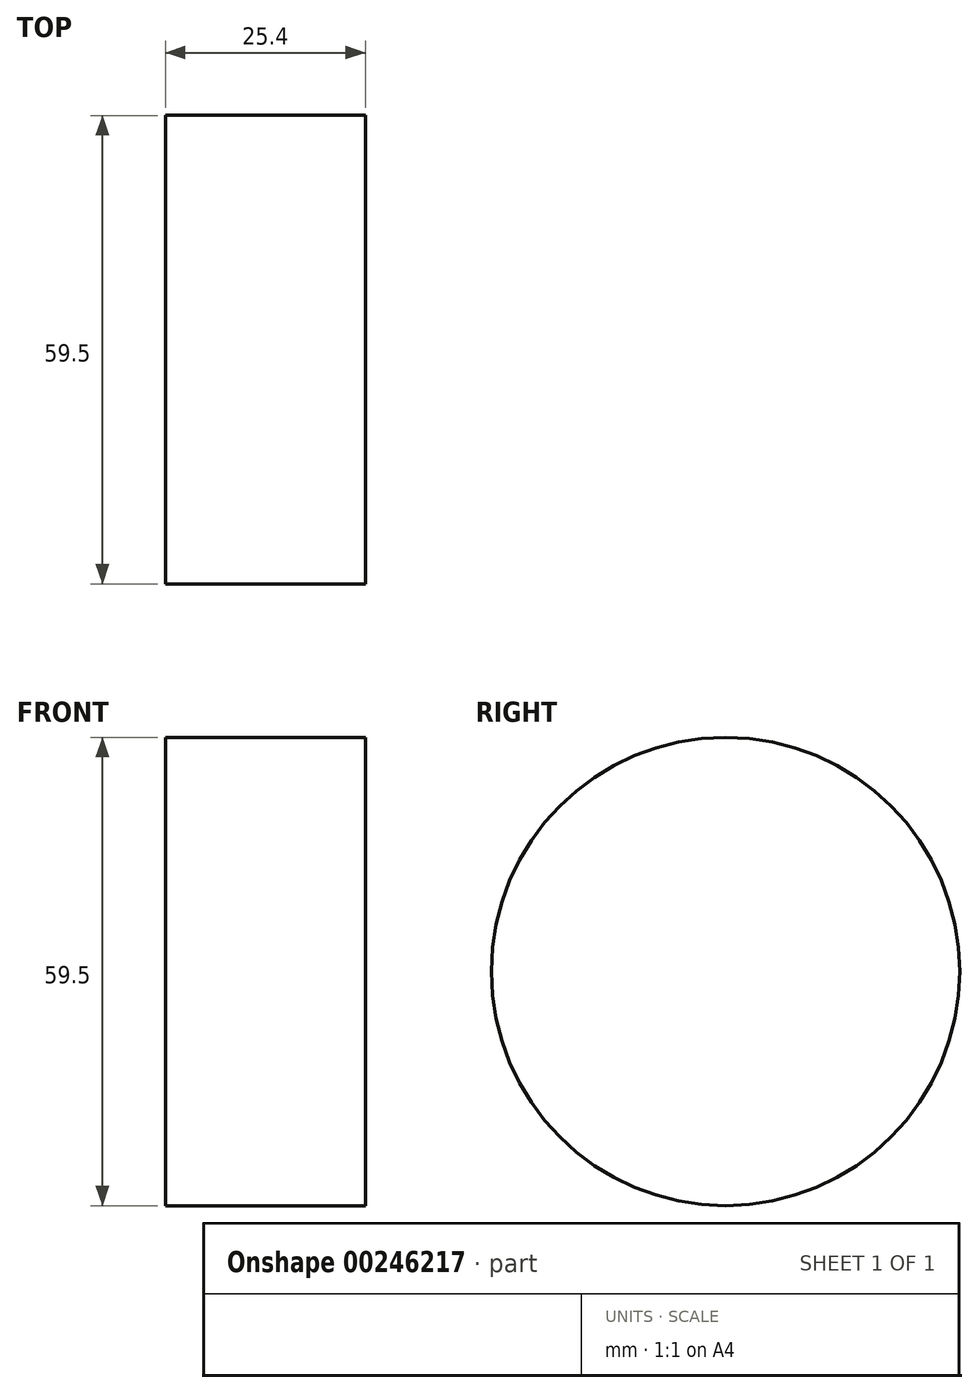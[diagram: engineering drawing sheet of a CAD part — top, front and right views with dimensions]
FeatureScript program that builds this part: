
annotation { "Feature Type Name" : "Feature", "Feature Type Description" : "" }
export const myFeature = defineFeature(function(context is Context, id is Id, definition is map)
    precondition{}
    {
        {
            var Q0;
            Q0=qCreatedBy(makeId("Right.planeOp"),FACE);
            var sketch = newSketch(context, id + "F0", { "sketchPlane" : qUnion([Q0])});
            skCircle(sketch, "E0", {"center": v(-39.35, 42.7) * mm, "radius": 29.75 * mm});
            skSolve(sketch);
        }
        {
            var Q0;
            Q0=makeQuery(id+"F0.imprint","IMPRINT",FACE,{"disambiguationData":[TD([[makeQuery(id+"F0.imprint","IMPRINT",EDGE,{"derivedFrom":sQuery(id+"F0.wireOp",EDGE,"E0")}),1.0]])]});
            extrude(context, id + "F1", {"entities" : qUnion([Q0]), "depth" : 25.4 * mm});
        }
    });
